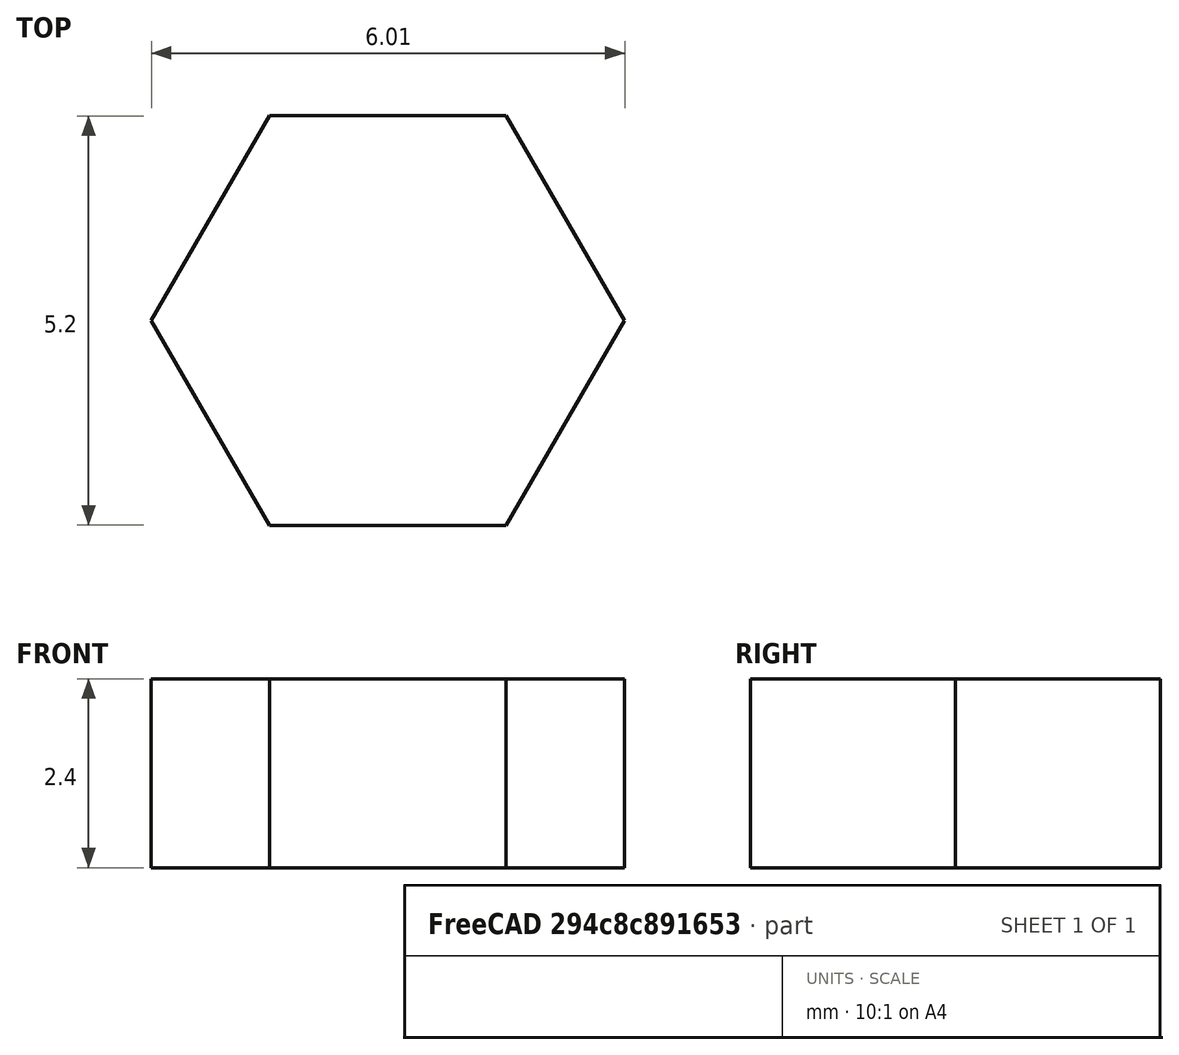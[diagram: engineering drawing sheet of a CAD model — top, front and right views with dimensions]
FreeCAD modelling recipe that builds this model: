
FCSTD DOCUMENT  (FreeCAD 0.21R0.20.1)
Label: Nut_DIN934_M3
License: All rights reserved
LicenseURL: https://en.wikipedia.org/wiki/All_rights_reserved
objects: Sketcher::SketchObject×1, Part::Extrusion×1
note: 2 computed .brp shape members not serialized (recipe doc carries the construction recipe); baked Part::Feature solids carry a one-line shape summary decoded from their .brp

FEATURE [Sketcher::SketchObject] Sketch
  FullyConstrained = true
  sketch-geometry (7):
    g0: LineSegment StartX=-3.005 StartY=0 StartZ=0 EndX=-1.5025 EndY=-2.60241 EndZ=0
    g1: LineSegment StartX=-1.5025 StartY=-2.60241 StartZ=0 EndX=1.5025 EndY=-2.60241 EndZ=0
    g2: LineSegment StartX=1.5025 StartY=-2.60241 StartZ=0 EndX=3.005 EndY=-9.7513e-12 EndZ=0
    g3: LineSegment StartX=3.005 StartY=-9.7512e-12 StartZ=0 EndX=1.5025 EndY=2.60241 EndZ=0
    g4: LineSegment StartX=1.5025 StartY=2.60241 StartZ=0 EndX=-1.5025 EndY=2.60241 EndZ=0
    g5: LineSegment StartX=-1.5025 StartY=2.60241 StartZ=0 EndX=-3.005 EndY=0 EndZ=0
    g6: Circle CenterX=0 CenterY=0 CenterZ=0 NormalX=0 NormalY=0 NormalZ=1 AngleXU=0 Radius=3.005
  constraints (16):
    c: Coincident(g0,g1)
    c: Coincident(g1,g2)
    c: Coincident(g2,g3)
    c: Coincident(g3,g4)
    c: Coincident(g4,g5)
    c: Coincident(g5,g0)
    c: Equal(g0, g1-g5) x5
    c: PointOnObject(g0,g6)
    c: PointOnObject(g1,g6)
    c: PointOnObject(g2,g6)
    c: PointOnObject(g3,g6)
    c: PointOnObject(g4,g6)
    c: PointOnObject(g5,g6)
    c: Coincident(g6,g-1)
    c: PointOnObject(g5,g-1)
    c: DistanceX(g0,g2) = 6.01
FEATURE [Part::Extrusion] Extrude  label="DIN934_M3"
  Base = -> Sketch
  Dir = (0,0,1)
  DirMode = 2
  FaceMakerClass = Part::FaceMakerBullseye
  LengthFwd = 2.4
  LengthRev = 0
  Solid = true
  Symmetric = false
